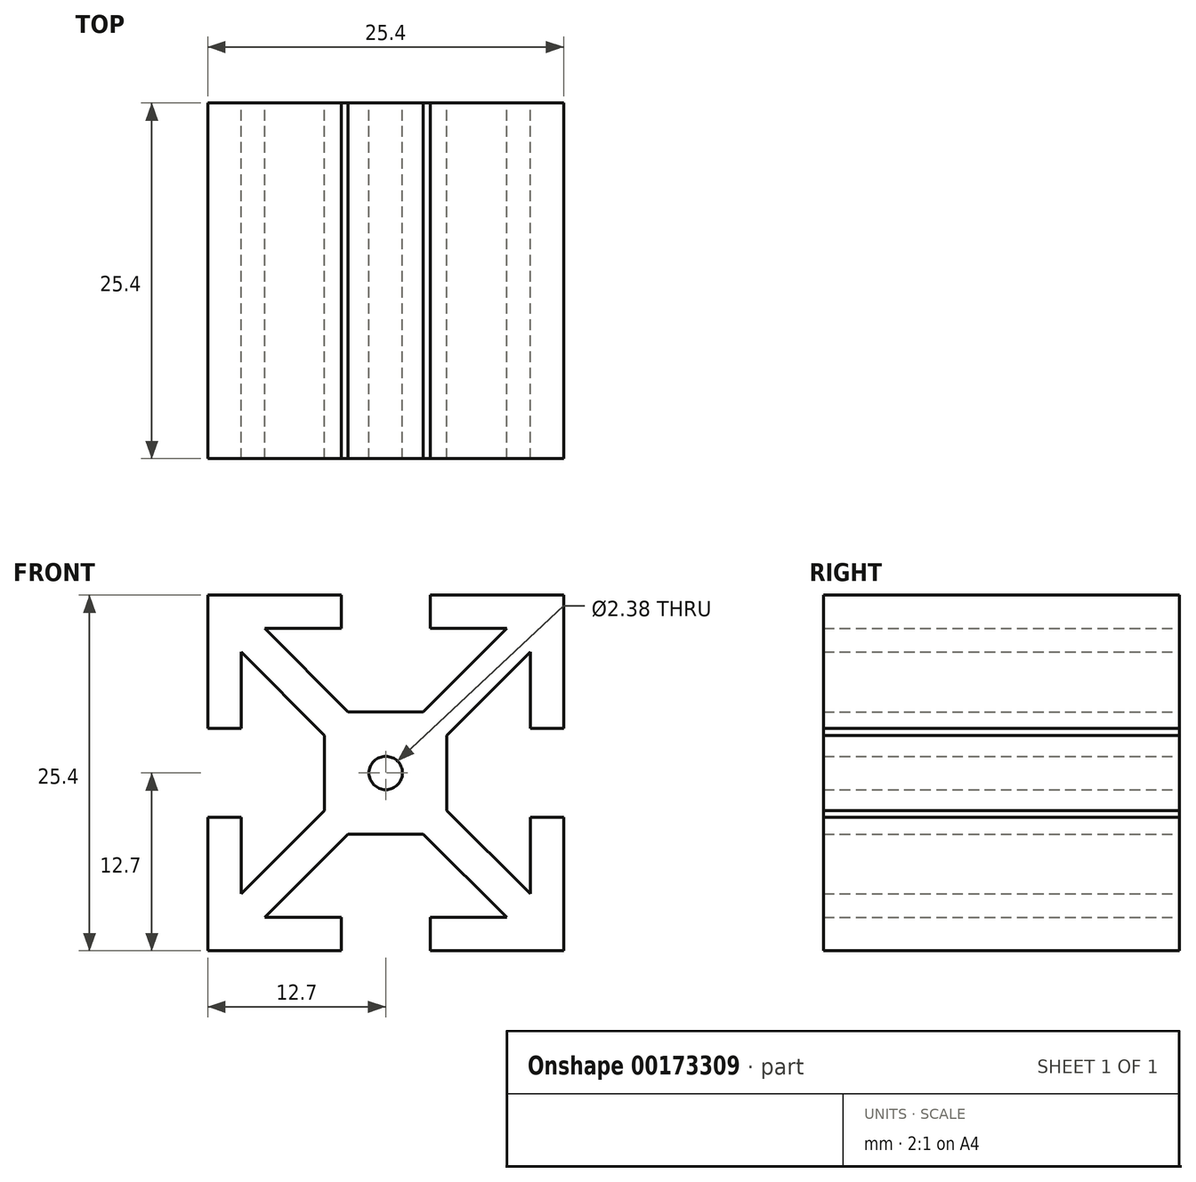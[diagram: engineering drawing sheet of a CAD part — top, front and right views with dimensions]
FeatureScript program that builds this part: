
annotation { "Feature Type Name" : "Feature", "Feature Type Description" : "" }
export const myFeature = defineFeature(function(context is Context, id is Id, definition is map)
    precondition{}
    {
        {
            var Q0;
            Q0=qCreatedBy(makeId("Front.planeOp"),FACE);
            var sketch = newSketch(context, id + "F0", { "sketchPlane" : qUnion([Q0])});
            skLineSegment(sketch, "E0.bottom", {"start": v(12.7, 12.7) * mm, "end": v(-12.7, 12.7) * mm});
            skLineSegment(sketch, "E0.top", {"start": v(12.7, -12.7) * mm, "end": v(-12.7, -12.7) * mm});
            skLineSegment(sketch, "E0.left", {"start": v(12.7, 12.7) * mm, "end": v(12.7, -12.7) * mm});
            skLineSegment(sketch, "E0.right", {"start": v(-12.7, 12.7) * mm, "end": v(-12.7, -12.7) * mm});
            skPoint(sketch, "E0.middle", {"position": v(0, 0) * mm});
            skLineSegment(sketch, "E1.bottom", {"start": v(10.32, 10.32) * mm, "end": v(-10.32, 10.32) * mm});
            skLineSegment(sketch, "E1.top", {"start": v(10.32, -10.32) * mm, "end": v(-10.32, -10.32) * mm});
            skLineSegment(sketch, "E1.left", {"start": v(10.32, 10.32) * mm, "end": v(10.32, -10.32) * mm});
            skLineSegment(sketch, "E1.right", {"start": v(-10.32, 10.32) * mm, "end": v(-10.32, -10.32) * mm});
            skLineSegment(sketch, "E2", {"start": v(8.63, 10.32) * mm, "end": v(10.32, 8.63) * mm});
            skLineSegment(sketch, "E3", {"start": v(-10.32, -8.63) * mm, "end": v(-8.63, -10.32) * mm});
            skLineSegment(sketch, "E4", {"start": v(-10.32, -8.63) * mm, "end": v(8.63, 10.32) * mm});
            skLineSegment(sketch, "E5", {"start": v(-8.63, -10.32) * mm, "end": v(10.32, 8.63) * mm});
            skLineSegment(sketch, "E6.MirrorCS", {"start": v(10.32, -8.63) * mm, "end": v(-8.63, 10.32) * mm});
            skLineSegment(sketch, "E7.MirrorCS", {"start": v(8.63, -10.32) * mm, "end": v(-10.32, 8.63) * mm});
            skLineSegment(sketch, "E8.MirrorCS", {"start": v(-8.63, 10.32) * mm, "end": v(-10.32, 8.63) * mm});
            skLineSegment(sketch, "E9.MirrorCS", {"start": v(10.32, -8.63) * mm, "end": v(8.63, -10.32) * mm});
            skCircle(sketch, "E10", {"center": v(0, 0) * mm, "radius": 1.2 * mm});
            skLineSegment(sketch, "E11.bottom", {"start": v(4.37, 4.37) * mm, "end": v(-4.37, 4.37) * mm});
            skLineSegment(sketch, "E11.top", {"start": v(4.37, -4.37) * mm, "end": v(-4.37, -4.37) * mm});
            skLineSegment(sketch, "E11.left", {"start": v(4.37, 4.37) * mm, "end": v(4.37, -4.37) * mm});
            skLineSegment(sketch, "E11.right", {"start": v(-4.37, 4.37) * mm, "end": v(-4.37, -4.37) * mm});
            skLineSegment(sketch, "E12", {"start": v(-3.17, 12.7) * mm, "end": v(-3.17, 10.32) * mm});
            skLineSegment(sketch, "E13", {"start": v(3.18, 12.7) * mm, "end": v(3.18, 10.32) * mm});
            skLineSegment(sketch, "E14.MirrorCS", {"start": v(-3.17, -12.7) * mm, "end": v(-3.17, -10.32) * mm});
            skLineSegment(sketch, "E15.MirrorCS", {"start": v(3.18, -12.7) * mm, "end": v(3.18, -10.32) * mm});
            skLineSegment(sketch, "E16", {"start": v(10.32, 3.18) * mm, "end": v(12.7, 3.18) * mm});
            skLineSegment(sketch, "E17", {"start": v(10.32, -3.18) * mm, "end": v(12.7, -3.18) * mm});
            skLineSegment(sketch, "E18.MirrorCS", {"start": v(-10.32, 3.18) * mm, "end": v(-12.7, 3.18) * mm});
            skLineSegment(sketch, "E19.MirrorCS", {"start": v(-10.32, -3.18) * mm, "end": v(-12.7, -3.18) * mm});
            skSolve(sketch);
        }
        {
            var Q0;
            {var subQ3=sQuery(id+"F0.wireOp",EDGE,"E12");Q0=makeQuery(id+"F0.imprint","IMPRINT",FACE,{"disambiguationData":[TD([[makeQuery(id+"F0.imprint","IMPRINT",EDGE,{"derivedFrom":subQ3}),-1.0]])]});}
            var Q1;
            {var subQ3=sQuery(id+"F0.wireOp",EDGE,"E13");Q1=makeQuery(id+"F0.imprint","IMPRINT",FACE,{"disambiguationData":[TD([[makeQuery(id+"F0.imprint","IMPRINT",EDGE,{"derivedFrom":subQ3}),1.0]])]});}
            var Q2;
            {var subQ3=sQuery(id+"F0.wireOp",EDGE,"E2");Q2=makeQuery(id+"F0.imprint","IMPRINT",FACE,{"disambiguationData":[TD([[makeQuery(id+"F0.imprint","IMPRINT",EDGE,{"derivedFrom":subQ3}),1.0]])]});}
            var Q3;
            {var subQ3=sQuery(id+"F0.wireOp",EDGE,"E8.MirrorCS");Q3=makeQuery(id+"F0.imprint","IMPRINT",FACE,{"disambiguationData":[TD([[makeQuery(id+"F0.imprint","IMPRINT",EDGE,{"derivedFrom":subQ3}),-1.0]])]});}
            var Q4;
            {var subQ5=sQuery(id+"F0.wireOp",EDGE,"E8.MirrorCS");Q4=makeQuery(id+"F0.imprint","IMPRINT",FACE,{"disambiguationData":[TD([[makeQuery(id+"F0.imprint","IMPRINT",EDGE,{"derivedFrom":subQ5}),1.0]])]});}
            var Q5;
            {var subQ6=sQuery(id+"F0.wireOp",EDGE,"E2");Q5=makeQuery(id+"F0.imprint","IMPRINT",FACE,{"disambiguationData":[TD([[makeQuery(id+"F0.imprint","IMPRINT",EDGE,{"derivedFrom":subQ6}),-1.0]])]});}
            var Q6;
            {var subQ0=sQuery(id+"F0.wireOp",EDGE,"E6.MirrorCS");var subQ1=sQuery(id+"F0.wireOp",EDGE,"E4");var subQ2=makeQuery(id+"F0.imprint","INTERSECT",VERTEX,{"derivedFrom":[subQ1,subQ0]});Q6=makeQuery(id+"F0.imprint","IMPRINT",FACE,{"disambiguationData":[TD([[makeQuery(id+"F0.imprint","IMPRINT",EDGE,{"disambiguationData":[TD([[subQ2,-1.0]])],"derivedFrom":subQ1}),1.0]])]});}
            var Q7;
            {var subQ0=sQuery(id+"F0.wireOp",EDGE,"E7.MirrorCS");var subQ1=sQuery(id+"F0.wireOp",EDGE,"E4");var subQ2=makeQuery(id+"F0.imprint","INTERSECT",VERTEX,{"derivedFrom":[subQ1,subQ0]});Q7=makeQuery(id+"F0.imprint","IMPRINT",FACE,{"disambiguationData":[TD([[makeQuery(id+"F0.imprint","IMPRINT",EDGE,{"disambiguationData":[TD([[subQ2,-1.0]])],"derivedFrom":subQ1}),1.0]])]});}
            var Q8;
            {var subQ0=sQuery(id+"F0.wireOp",EDGE,"E11.right");var subQ1=sQuery(id+"F0.wireOp",EDGE,"E4");var subQ2=makeQuery(id+"F0.imprint","INTERSECT",VERTEX,{"derivedFrom":[subQ1,subQ0]});Q8=makeQuery(id+"F0.imprint","IMPRINT",FACE,{"disambiguationData":[TD([[makeQuery(id+"F0.imprint","IMPRINT",EDGE,{"disambiguationData":[TD([[subQ2,-1.0]])],"derivedFrom":subQ1}),1.0]])]});}
            var Q9;
            {var subQ0=sQuery(id+"F0.wireOp",EDGE,"E11.top");var subQ1=sQuery(id+"F0.wireOp",EDGE,"E5");var subQ2=makeQuery(id+"F0.imprint","INTERSECT",VERTEX,{"derivedFrom":[subQ1,subQ0]});Q9=makeQuery(id+"F0.imprint","IMPRINT",FACE,{"disambiguationData":[TD([[makeQuery(id+"F0.imprint","IMPRINT",EDGE,{"disambiguationData":[TD([[subQ2,-1.0]])],"derivedFrom":subQ1}),-1.0]])]});}
            var Q10;
            {var subQ0=sQuery(id+"F0.wireOp",EDGE,"E6.MirrorCS");var subQ1=sQuery(id+"F0.wireOp",EDGE,"E5");var subQ2=makeQuery(id+"F0.imprint","INTERSECT",VERTEX,{"derivedFrom":[subQ1,subQ0]});Q10=makeQuery(id+"F0.imprint","IMPRINT",FACE,{"disambiguationData":[TD([[makeQuery(id+"F0.imprint","IMPRINT",EDGE,{"disambiguationData":[TD([[subQ2,-1.0]])],"derivedFrom":subQ1}),-1.0]])]});}
            var Q11;
            {var subQ0=sQuery(id+"F0.wireOp",EDGE,"E6.MirrorCS");var subQ7=sQuery(id+"F0.wireOp",EDGE,"E4");var subQ10=makeQuery(id+"F0.imprint","INTERSECT",VERTEX,{"derivedFrom":[subQ7,subQ0]});Q11=makeQuery(id+"F0.imprint","IMPRINT",FACE,{"disambiguationData":[TD([[makeQuery(id+"F0.imprint","IMPRINT",EDGE,{"disambiguationData":[TD([[subQ10,-1.0]])],"derivedFrom":subQ7}),-1.0]])]});}
            var Q12;
            {var subQ1=sQuery(id+"F0.wireOp",EDGE,"E5");var subQ6=sQuery(id+"F0.wireOp",EDGE,"E7.MirrorCS");var subQ7=makeQuery(id+"F0.imprint","INTERSECT",VERTEX,{"derivedFrom":[subQ1,subQ6]});Q12=makeQuery(id+"F0.imprint","IMPRINT",FACE,{"disambiguationData":[TD([[makeQuery(id+"F0.imprint","IMPRINT",EDGE,{"disambiguationData":[TD([[subQ7,-1.0]])],"derivedFrom":subQ1}),-1.0]])]});}
            var Q13;
            {var subQ1=sQuery(id+"F0.wireOp",EDGE,"E4");var subQ8=sQuery(id+"F0.wireOp",EDGE,"E11.right");var subQ10=makeQuery(id+"F0.imprint","INTERSECT",VERTEX,{"derivedFrom":[subQ1,subQ8]});Q13=makeQuery(id+"F0.imprint","IMPRINT",FACE,{"disambiguationData":[TD([[makeQuery(id+"F0.imprint","IMPRINT",EDGE,{"disambiguationData":[TD([[subQ10,-1.0]])],"derivedFrom":subQ1}),-1.0]])]});}
            var Q14;
            {var subQ6=sQuery(id+"F0.wireOp",EDGE,"E3");Q14=makeQuery(id+"F0.imprint","IMPRINT",FACE,{"disambiguationData":[TD([[makeQuery(id+"F0.imprint","IMPRINT",EDGE,{"derivedFrom":subQ6}),1.0]])]});}
            var Q15;
            {var subQ5=sQuery(id+"F0.wireOp",EDGE,"E9.MirrorCS");Q15=makeQuery(id+"F0.imprint","IMPRINT",FACE,{"disambiguationData":[TD([[makeQuery(id+"F0.imprint","IMPRINT",EDGE,{"derivedFrom":subQ5}),-1.0]])]});}
            var Q16;
            {var subQ3=sQuery(id+"F0.wireOp",EDGE,"E15.MirrorCS");Q16=makeQuery(id+"F0.imprint","IMPRINT",FACE,{"disambiguationData":[TD([[makeQuery(id+"F0.imprint","IMPRINT",EDGE,{"derivedFrom":subQ3}),-1.0]])]});}
            var Q17;
            {var subQ5=sQuery(id+"F0.wireOp",EDGE,"E14.MirrorCS");Q17=makeQuery(id+"F0.imprint","IMPRINT",FACE,{"disambiguationData":[TD([[makeQuery(id+"F0.imprint","IMPRINT",EDGE,{"derivedFrom":subQ5}),1.0]])]});}
            var Q18;
            {var subQ3=sQuery(id+"F0.wireOp",EDGE,"E9.MirrorCS");Q18=makeQuery(id+"F0.imprint","IMPRINT",FACE,{"disambiguationData":[TD([[makeQuery(id+"F0.imprint","IMPRINT",EDGE,{"derivedFrom":subQ3}),1.0]])]});}
            var Q19;
            {var subQ3=sQuery(id+"F0.wireOp",EDGE,"E3");Q19=makeQuery(id+"F0.imprint","IMPRINT",FACE,{"disambiguationData":[TD([[makeQuery(id+"F0.imprint","IMPRINT",EDGE,{"derivedFrom":subQ3}),-1.0]])]});}
            var Q20;
            {var subQ0=sQuery(id+"F0.wireOp",EDGE,"E10");var subQ1=sQuery(id+"F0.wireOp",EDGE,"E5");var subQ2=makeQuery(id+"F0.imprint","INTERSECT",VERTEX,{"derivedFrom":[subQ1,subQ0]});Q20=makeQuery(id+"F0.imprint","IMPRINT",FACE,{"disambiguationData":[TD([[makeQuery(id+"F0.imprint","IMPRINT",EDGE,{"disambiguationData":[TD([[subQ2,-1.0]])],"derivedFrom":subQ1}),1.0]])]});}
            var Q21;
            {var subQ0=sQuery(id+"F0.wireOp",EDGE,"E7.MirrorCS");var subQ1=sQuery(id+"F0.wireOp",EDGE,"E5");var subQ2=makeQuery(id+"F0.imprint","INTERSECT",VERTEX,{"derivedFrom":[subQ1,subQ0]});Q21=makeQuery(id+"F0.imprint","IMPRINT",FACE,{"disambiguationData":[TD([[makeQuery(id+"F0.imprint","IMPRINT",EDGE,{"disambiguationData":[TD([[subQ2,-1.0]])],"derivedFrom":subQ1}),1.0]])]});}
            var Q22;
            {var subQ0=sQuery(id+"F0.wireOp",EDGE,"E7.MirrorCS");var subQ1=sQuery(id+"F0.wireOp",EDGE,"E4");var subQ2=makeQuery(id+"F0.imprint","INTERSECT",VERTEX,{"derivedFrom":[subQ1,subQ0]});Q22=makeQuery(id+"F0.imprint","IMPRINT",FACE,{"disambiguationData":[TD([[makeQuery(id+"F0.imprint","IMPRINT",EDGE,{"disambiguationData":[TD([[subQ2,-1.0]])],"derivedFrom":subQ1}),-1.0]])]});}
            var Q23;
            {var subQ0=sQuery(id+"F0.wireOp",EDGE,"E10");var subQ1=sQuery(id+"F0.wireOp",EDGE,"E4");var subQ2=makeQuery(id+"F0.imprint","INTERSECT",VERTEX,{"derivedFrom":[subQ1,subQ0]});Q23=makeQuery(id+"F0.imprint","IMPRINT",FACE,{"disambiguationData":[TD([[makeQuery(id+"F0.imprint","IMPRINT",EDGE,{"disambiguationData":[TD([[subQ2,-1.0]])],"derivedFrom":subQ1}),-1.0]])]});}
            extrude(context, id + "F1", {"entities" : qUnion([Q0, Q1, Q2, Q3, Q4, Q5, Q6, Q7, Q8, Q9, Q10, Q11, Q12, Q13, Q14, Q15, Q16, Q17, Q18, Q19, Q20, Q21, Q22, Q23]), "depth" : 25.4 * mm});
        }
    });
